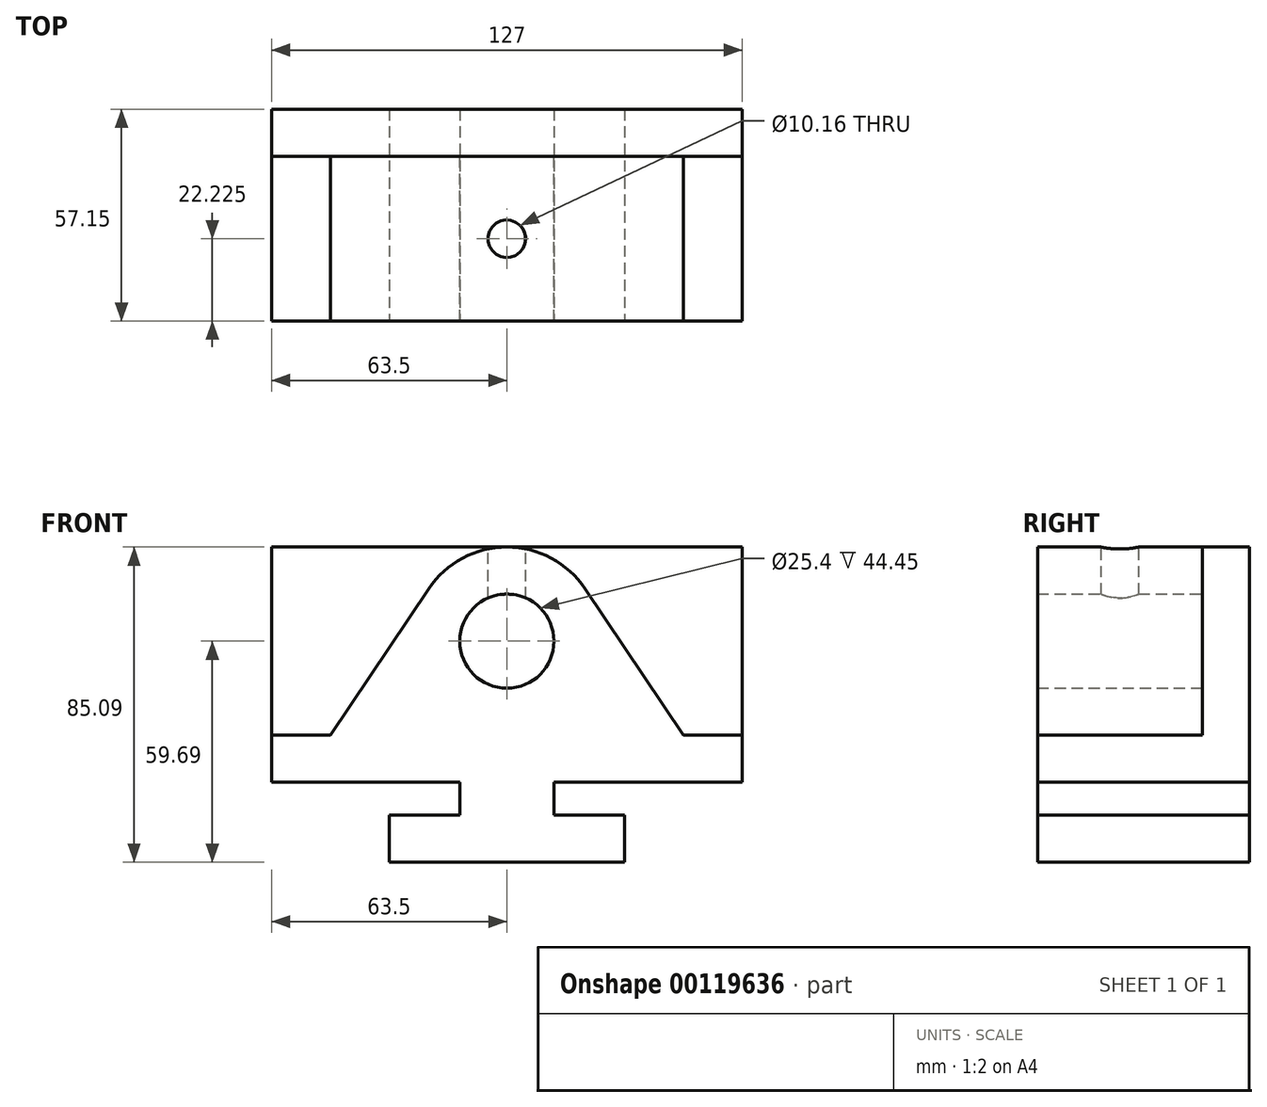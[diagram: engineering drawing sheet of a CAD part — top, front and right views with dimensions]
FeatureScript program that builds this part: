
annotation { "Feature Type Name" : "Feature", "Feature Type Description" : "" }
export const myFeature = defineFeature(function(context is Context, id is Id, definition is map)
    precondition{}
    {
        {
            var Q0;
            Q0=qCreatedBy(makeId("Right.planeOp"),FACE);
            var sketch = newSketch(context, id + "F0", { "sketchPlane" : qUnion([Q0])});
            skLineSegment(sketch, "E0", {"start": v(0, 0) * mm, "end": v(0, 63.5) * mm});
            skLineSegment(sketch, "E1", {"start": v(0, 63.5) * mm, "end": v(-12.7, 63.5) * mm});
            skLineSegment(sketch, "E2", {"start": v(-12.7, 63.5) * mm, "end": v(-12.7, 12.7) * mm});
            skLineSegment(sketch, "E3", {"start": v(-12.7, 12.7) * mm, "end": v(-57.15, 12.7) * mm});
            skLineSegment(sketch, "E4", {"start": v(-57.15, 12.7) * mm, "end": v(-57.15, 0) * mm});
            skLineSegment(sketch, "E5", {"start": v(-57.15, 0) * mm, "end": v(0, 0) * mm});
            skSolve(sketch);
        }
        {
            var Q0;
            Q0 = qSketchRegion(id + "F0", true);
            extrude(context, id + "F1", {"entities" : qUnion([Q0]), "oppositeDirection" : true, "depth" : 127 * mm});
        }
        {
            var Q0;
            Q0=makeQuery(id+"F1.opExtrude","SWEPT_FACE",FACE,{"disambiguationData":[OSD([sQuery(id+"F0.wireOp",EDGE,"E4")])]});
            var sketch = newSketch(context, id + "F2", { "sketchPlane" : qUnion([Q0])});
            skLineSegment(sketch, "E6", {"start": v(-63.5, 0) * mm, "end": v(-50.8, 0) * mm});
            skLineSegment(sketch, "E7", {"start": v(-50.8, 0) * mm, "end": v(-50.8, -8.89) * mm});
            skLineSegment(sketch, "E8", {"start": v(-50.8, -8.89) * mm, "end": v(-31.75, -8.89) * mm});
            skLineSegment(sketch, "E9", {"start": v(-31.75, -8.9) * mm, "end": v(-31.75, -21.59) * mm});
            skLineSegment(sketch, "E10", {"start": v(-31.75, -21.59) * mm, "end": v(-95.25, -21.59) * mm});
            skLineSegment(sketch, "E11", {"start": v(-95.25, -21.59) * mm, "end": v(-95.25, -8.9) * mm});
            skLineSegment(sketch, "E12", {"start": v(-95.25, -8.89) * mm, "end": v(-76.2, -8.89) * mm});
            skLineSegment(sketch, "E13", {"start": v(-76.2, -8.89) * mm, "end": v(-76.2, 0) * mm});
            skLineSegment(sketch, "E14", {"start": v(-76.2, 0) * mm, "end": v(-63.5, 0) * mm});
            skSolve(sketch);
        }
        {
            var Q0;
            Q0 = qSketchRegion(id + "F2", true);
            extrude(context, id + "F3", {"entities" : qUnion([Q0]), "operationType" : NewBodyOperationType.ADD, "oppositeDirection" : true, "depth" : 57.15 * mm});
        }
        {
            var Q0;
            Q0=makeQuery(id+"F1.opExtrude","SWEPT_FACE",FACE,{"disambiguationData":[OSD([sQuery(id+"F0.wireOp",EDGE,"E2")])]});
            var sketch = newSketch(context, id + "F4", { "sketchPlane" : qUnion([Q0])});
            skLineSegment(sketch, "E15", {"start": v(0, 12.7) * mm, "end": v(-15.88, 12.7) * mm, "construction": true});
            skLineSegment(sketch, "E16", {"start": v(-15.87, 12.7) * mm, "end": v(-42.4, 52.25) * mm});
            skLineSegment(sketch, "E17", {"start": v(-127, 12.7) * mm, "end": v(-111.12, 12.7) * mm, "construction": true});
            skLineSegment(sketch, "E18", {"start": v(-111.13, 12.7) * mm, "end": v(-84.6, 52.25) * mm});
            skArc(sketch, "E19", {"start": v(-42.4, 52.25) * mm, "mid": v(-63.5, 63.5) * mm, "end": v(-84.6, 52.25) * mm});
            skLineSegment(sketch, "E20", {"start": v(-111.12, 12.7) * mm, "end": v(-15.88, 12.7) * mm});
            skCircle(sketch, "E21", {"center": v(-63.5, 38.1) * mm, "radius": 12.7 * mm});
            skSolve(sketch);
        }
        {
            var Q0;
            Q0 = qSketchRegion(id + "F4", true);
            var Q1;
            Q1=makeQuery(id+"F3.boolean.opBoolean","MERGE",FACE,{"derivedFrom":[makeQuery(id+"F1.opExtrude","SWEPT_FACE",FACE,{"disambiguationData":[OSD([sQuery(id+"F0.wireOp",EDGE,"E4")])]}),makeQuery(id+"F3.opExtrude","CAP_FACE",FACE,{"disambiguationData":[OSD([sQuery(id+"F2.wireOp",EDGE,"E6"),sQuery(id+"F2.wireOp",EDGE,"E7"),sQuery(id+"F2.wireOp",EDGE,"E8"),sQuery(id+"F2.wireOp",EDGE,"E9"),sQuery(id+"F2.wireOp",EDGE,"E10"),sQuery(id+"F2.wireOp",EDGE,"E11"),sQuery(id+"F2.wireOp",EDGE,"E12"),sQuery(id+"F2.wireOp",EDGE,"E13"),sQuery(id+"F2.wireOp",EDGE,"E14")])],"isStart":true})]});
            extrude(context, id + "F5", {"entities" : qUnion([Q0]), "operationType" : NewBodyOperationType.ADD, "endBound" : BoundingType.UP_TO_SURFACE, "endBoundEntityFace" : qUnion([Q1]), "depth" : 25.4 * mm});
        }
        {
            var Q0;
            Q0=makeQuery(id+"F1.opExtrude","SWEPT_FACE",FACE,{"disambiguationData":[OSD([sQuery(id+"F0.wireOp",EDGE,"E1")])]});
            var sketch = newSketch(context, id + "F6", { "sketchPlane" : qUnion([Q0])});
            skLineSegment(sketch, "E22", {"start": v(-63.5, 0) * mm, "end": v(-63.5, -34.93) * mm, "construction": true});
            skCircle(sketch, "E23", {"center": v(-63.5, -34.93) * mm, "radius": 5.08 * mm});
            skSolve(sketch);
        }
        {
            var Q0;
            Q0 = qSketchRegion(id + "F6", true);
            extrude(context, id + "F7", {"entities" : qUnion([Q0]), "operationType" : NewBodyOperationType.REMOVE, "endBound" : BoundingType.UP_TO_NEXT, "oppositeDirection" : true, "depth" : 25.4 * mm});
        }
    });
